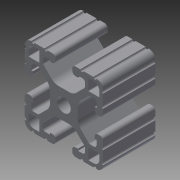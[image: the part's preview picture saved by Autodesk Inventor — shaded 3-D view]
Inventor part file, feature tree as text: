
AUTODESK INVENTOR PART (.ipt)
format: ipt  version: 2013 (Build 170138000, 138)  size: 308,224 bytes
history: native  units: in
note: dims shown in document units (in); Inventor stores cm internally (conversion verified against a paired STEP export)
features: extrude x1, sketch x1
ambient origin geometry x8: Origin, YZ Plane, XZ Plane, XY Plane, X Axis, Y Axis, Z Axis, Center Point
bodies: Solid1 (feature_tree)
feature tree (2):
  extrude  "Extrusion1"  [1 undecoded]
  sketch  "Sketch1"  dims[d0=1.0in d1=0.0in]
note: 1 required parameter value undecoded (feature->parameter linkage not recoverable at this tier; creation-order binding heuristic only, values carry confidence <= 0.55)
